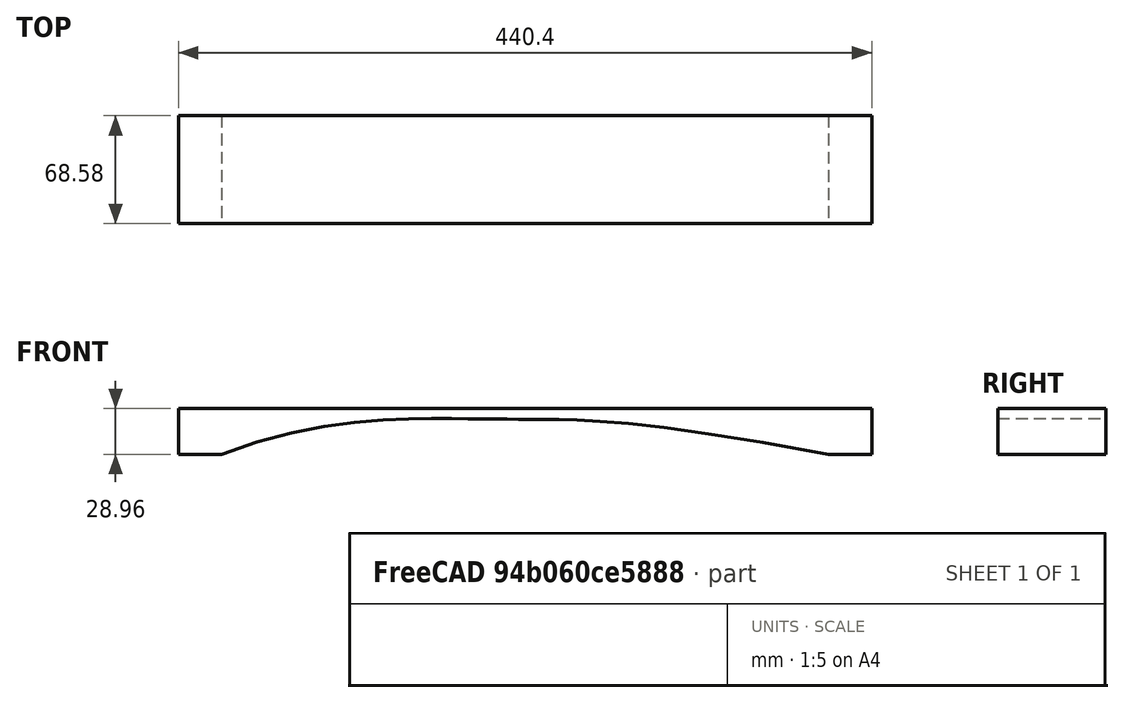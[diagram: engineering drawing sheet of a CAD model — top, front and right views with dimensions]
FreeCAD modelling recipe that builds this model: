
FCSTD DOCUMENT  (FreeCAD 0.20R29410 (Git))
Label: Chestnut-0.82-Bar
License: All rights reserved
LicenseURL: http://en.wikipedia.org/wiki/All_rights_reserved
objects: Fem::FemResultObjectPython×9, Fem::FemPostWarpVectorFilter×3, Fem::FemPostDataAtPointFilter×3, Fem::FemPostPipeline×3, Sketcher::SketchObject×1, Part::Extrusion×1, Fem::FemSolverObjectPython×1, App::MaterialObjectPython×1, Fem::ConstraintDisplacement×1, Fem::FemMeshShapeNetgenObject×1, Fem::FemMeshObjectPython×1, App::TextDocument×1, Fem::FemAnalysis×1
note: 2 computed .brp shape members not serialized (recipe doc carries the construction recipe); baked Part::Feature solids carry a one-line shape summary decoded from their .brp

FEATURE [Sketcher::SketchObject] Sketch
  FullyConstrained = true
  Placement = pos=(0,0,0) rot=(1,0,0;1.5708rad)
  sketch-geometry (12):
    g0: LineSegment StartX=27.53 StartY=0 StartZ=0 EndX=0 EndY=0 EndZ=0
    g1: LineSegment StartX=0 StartY=0 StartZ=0 EndX=0 EndY=28.96 EndZ=0
    g2: LineSegment StartX=0 StartY=28.96 StartZ=0 EndX=440.4 EndY=28.96 EndZ=0
    g3: LineSegment StartX=440.4 StartY=28.96 StartZ=0 EndX=440.4 EndY=0 EndZ=0
    g4: LineSegment StartX=440.4 StartY=0 StartZ=0 EndX=412.87 EndY=0 EndZ=0
    g5-g10: Circle x6 (B-spline internal-alignment scaffolding for g11; pole/knot coordinates omitted)
    g11: BSplineCurve PolesCount=6 KnotsCount=4 Degree=3 IsPeriodic=0
  constraints (38):
    c: DistanceX(g0) = 0
    c: DistanceY(g0) = 0
    c: Distance(g1,g1) = 28.96
    c: Distance(g2,g2) = 440.4
    c: DistanceX(g0,g0) = 27.53
    c: DistanceX(g4,g4) = 27.53
    c: Horizontal(g0)
    c: Vertical(g1)
    c: Horizontal(g2)
    c: Vertical(g3)
    c: Horizontal(g4)
    c: Equal(g3,g1)
    c: Coincident(g0,g1)
    c: Coincident(g1,g2)
    c: Coincident(g2,g3)
    c: Coincident(g3,g4)
    c: DistanceX(g6) = 296.2
    c: DistanceY(g6) = 21.75
    c: DistanceX(g7) = 221.63
    c: DistanceY(g7) = 21.99
    c: DistanceX(g8) = 190.19
    c: DistanceY(g8) = 22.68
    c: DistanceX(g9) = 86.07
    c: DistanceY(g9) = 22.89
    c: Weight(g5) = 1
    c: InternalAlignment(g5,g11)
    c: Weight(g6) = 1
    c: InternalAlignment(g6,g11)
    c: Weight(g7) = 1
    c: InternalAlignment(g7,g11)
    c: Weight(g8) = 1
    c: InternalAlignment(g8,g11)
    c: Weight(g9) = 1
    c: InternalAlignment(g9,g11)
    c: Weight(g10) = 1
    c: InternalAlignment(g10,g11)
    c: Coincident(g4,g11)
    c: Coincident(g0,g11)
FEATURE [Part::Extrusion] Bar
  Base = -> Sketch
  Dir = (0,-1,-3e-16)
  DirMode = 2
  FaceMakerClass = Part::FaceMakerBullseye
  LengthFwd = 68.58
  LengthRev = 0
  Solid = true
  Symmetric = false
FEATURE [Fem::FemSolverObjectPython] SolverCcxTools  # FEM object (typed FeaturePython)
  AnalysisType = 1
  BeamShellResultOutput3D = false
  BucklingFactors = 1
  EigenmodeHighLimit = 20000
  EigenmodeLowLimit = 20
  EigenmodesCount = 12
  GeometricalNonlinearity = 0
  IterationsControlParameterCutb = 0.25,0.5,0.75,0.85,,,1.5,
  IterationsControlParameterIter = 4,8,9,200,10,400,,200,,
  IterationsControlParameterTimeUse = false
  IterationsThermoMechMaximum = 2000
  IterationsUserDefinedIncrementations = false
  IterationsUserDefinedTimeStepLength = false
  MaterialNonlinearity = 0
  MatrixSolverType = 0
  SplitInputWriter = false
  ThermoMechSteadyState = false
  TimeEnd = 1
  TimeInitialStep = 0.01
FEATURE [App::MaterialObjectPython] MaterialSolid  # material (typed FeaturePython)
  Category = 0
  Material = CompressiveStrength=4300 kPa; Density=430 kg/m^3; Name=Wood-Chestnut; PoissonRatio=0.32; ShearModulus=7.4 MPa; UltimateTensileStrength=59.0 MPa; YoungsModulus=8500 MPa
FEATURE [Fem::ConstraintDisplacement] FemConstraintDisplacement
  NormalDirection = (0,3e-16,-1)
  Normals = (118) [(0,3.3e-16,-1),(0,3.3e-16,-1),(0,3.3e-16,-1),(0,3.3e-16,-1),(0,3.3e-16,-1),(0,3.3e-16,-1),(0,3.3e-16,-1),(0,3.3e-16,-1),(0,3.3e-16,-1),(0,3.3e-16,-1),+108 more]
  Points = (118) [(27.53,-68.58,-2.26314e-14),(18.3533,-68.58,-2.26314e-14),(9.17667,-68.58,-2.26314e-14),(0,-68.58,-2.26314e-14),(27.53,-45.72,-1.50876e-14),+113 more]
  References = -> [Bar]
  rotxFix = false
  rotxFree = true
  rotyFix = false
  rotyFree = true
  rotzFix = false
  rotzFree = true
  xDisplacement = 0
  xFix = false
  xFree = true
  xRotation = 0
  yDisplacement = 0
  yFix = true
  yFree = false
  yRotation = 0
  zDisplacement = 0
  zFix = false
  zFree = true
  zRotation = 0
FEATURE [Fem::FemMeshShapeNetgenObject] FEMMeshNetgen
  Fineness = 4
  GrowthRate = 0.3
  MaxSize = 10
  NbSegsPerEdge = 1
  NbSegsPerRadius = 2
  Optimize = true
  SecondOrder = true
  Shape = -> Bar
FEATURE [Fem::FemMeshObjectPython] ResultMesh  # FEM object (typed FeaturePython)
FEATURE [Fem::FemResultObjectPython] CCX_EigenMode_4_Results  # FEM object (typed FeaturePython)
  DisplacementLengths = [66.8075,66.8075,97.2391,97.2391,92.7353,92.7354,104.217,104.217,111.02,111.02,73.6046,73.6047,85.9113,98.3192,106.859,104.538,89.1303,74.1174,59.119,44.0852,29.1952,14.611,5.08468,16.9677,31.471,46.0865,60.4038,74.2639,87.4492,99.5208,+5591 more]
  DisplacementVectors = (5621) [(29.6396,0,59.8727),(29.6396,0,59.8727),(29.6413,0,92.6112),(29.6414,0,92.6112),(-4.79638,0,92.6112),(-4.79642,0,92.6113),(4.97997,0,104.098),+5614 more]
  Eigenmode = 4
  EigenmodeFrequency = 130.83
  MaxShear = [0.793623,0.833442,0.0306815,0.0297045,0.0575452,0.0573412,0.0387805,0.0310506,0.0286361,0.026426,0.681681,0.640425,0.447118,0.128415,0.0679354,0.0973531,0.108643,0.634201,1.60297,3.41101,6.19905,11.583,18.5669,29.2026,45.2438,67.8662,+5595 more]
  Mesh = -> ResultMesh
  NodeNumbers = [1,2,3,4,5,6,7,8,9,10,11,12,13,14,15,16,17,18,19,20,21,22,23,24,25,26,27,28,29,30,31,32,33,34,35,36,37,38,39,40,41,42,43,44,45,46,47,48,49,50,51,52,53,54,55,56,57,58,59,60,61,62,63,64,65,66,67,68,69,+5552 more]
  NodeStrainXX = [0.000162708,0.000169979,-1.07884e-06,-1.07332e-06,-4.70892e-07,-3.62167e-08,8.78541e-07,1.2473e-06,-8.06536e-07,-6.19092e-07,0.000132596,0.000125552,9.50642e-05,2.62909e-05,3.89215e-06,-8.18627e-06,-2.10946e-05,-0.000130126,-0.000334274,+5602 more]
  NodeStrainXY = [-3.87351e-07,-1.91961e-06,6.93051e-07,-5.99991e-07,-1.79433e-07,9.33019e-08,1.69973e-06,-7.83592e-07,-6.94631e-07,8.3591e-07,-5.42509e-07,1.34477e-06,5.06708e-07,6.29561e-09,4.11864e-07,-1.75556e-06,2.84822e-07,1.27065e-06,7.13435e-06,+5602 more]
  NodeStrainXZ = [-2.8685e-05,-2.84597e-05,-4.64503e-06,-4.52092e-06,-8.56091e-06,-8.6366e-06,5.67135e-06,4.67326e-06,4.29e-06,3.89002e-06,3.61949e-05,3.31665e-05,-2.03295e-06,-4.86228e-06,-7.29797e-06,-7.9659e-06,-7.52187e-06,-1.24326e-05,-3.20836e-05,+5602 more]
  NodeStrainYY = [-2.29518e-12,5.81513e-12,0,0,-2.14727e-12,-3.46024e-15,0,0,0,0,-3.38509e-12,-3.00784e-12,2.09083e-07,-5.76141e-07,-6.02025e-08,1.30288e-13,3.25778e-12,1.25115e-07,3.93909e-07,-2.69759e-11,2.80364e-11,-2.59318e-05,-9.41e-06,-1.5324e-05,+5597 more]
  NodeStrainYZ = [-3.50751e-07,-1.51215e-06,-4.74264e-07,3.68907e-07,6.61863e-08,-1.53237e-08,-2.48968e-07,6.46807e-07,-5.76628e-07,6.47043e-07,1.21666e-06,-1.60203e-07,-6.62246e-07,-6.41747e-07,7.67443e-07,1.53127e-06,-2.16566e-06,8.19819e-07,-4.53612e-06,+5602 more]
  NodeStrainZZ = [-7.70098e-05,-8.249e-05,-1.86474e-06,-1.84357e-06,4.64207e-06,4.29724e-06,2.49195e-06,1.6006e-06,-1.84808e-06,-1.67572e-06,-6.63414e-05,-6.19546e-05,-4.37331e-05,-1.23557e-05,-1.12699e-05,1.71027e-05,8.6202e-06,6.52526e-05,0.000159143,+5602 more]
  NodeStressXX = [1.53827,1.59534,-0.0237959,-0.0236076,0.0208432,0.0241565,0.0249496,0.024333,-0.0203884,-0.0171219,1.23307,1.1725,0.907168,0.245764,-0.0175109,-0.00167765,-0.207238,-1.20854,-3.1527,-6.65105,-12.3436,-22.519,-36.3695,-57.4007,-89.5534,+5596 more]
  NodeStressXY = [-0.00249431,-0.0123611,0.00446283,-0.00386358,-0.00115544,0.000600808,0.0109452,-0.00504586,-0.00447301,0.00538275,-0.00349343,0.00865947,0.00326289,4.05399e-05,0.00265215,-0.0113047,0.00183408,0.00818224,0.0459409,-0.0196225,-0.071634,+5600 more]
  NodeStressXZ = [-0.184714,-0.183263,-0.0299112,-0.029112,-0.0551271,-0.0556144,0.03652,0.0300929,0.027625,0.0250493,0.233073,0.213572,-0.013091,-0.0313101,-0.0469945,-0.0512956,-0.0484363,-0.0800581,-0.206599,-0.107018,-0.383565,-2.88037,-5.68835,-8.86154,+5597 more]
  NodeStressYY = [0.490529,0.500779,-0.0168488,-0.016696,0.0238754,0.0243897,0.0192924,0.0163011,-0.0151948,-0.0131353,0.379234,0.364024,0.296358,0.0727561,-0.0429617,0.051037,-0.071402,-0.369807,-0.997644,-2.07487,-3.94135,-7.45487,-12.0454,-19.0587,+5597 more]
  NodeStressYZ = [-0.00225863,-0.00973732,-0.00305397,0.00237554,0.000426199,-9.86756e-05,-0.0016032,0.00416505,-0.00371313,0.00416657,0.00783455,-0.00103161,-0.00426446,-0.00413246,0.00494186,0.00986046,-0.0139455,0.00527914,-0.0292099,0.0309938,-0.114886,+5600 more]
  NodeStressZZ = [-0.00536748,-0.0304064,-0.0288566,-0.0285675,0.0537675,0.0520614,0.035339,0.026608,-0.0270953,-0.0239259,-0.0479645,-0.0349264,0.0133971,-0.00309685,-0.115145,0.161168,-0.0158931,0.0495748,0.0246048,0.167091,0.0268859,-0.0886269,-1.02233,+5598 more]
  PrincipalMax = [1.56007,1.61586,0.0050034,0.00408445,0.094853,0.0954496,0.0677832,0.0555914,0.00570159,0.00704383,1.27416,1.20925,0.907378,0.249644,0.00144179,0.177242,-0.00152922,0.0547019,0.0389779,0.169207,0.0419516,0.28008,-0.129444,-0.373552,-0.60558,+5596 more]
  PrincipalMed = [0.490537,0.500887,-0.0181452,-0.0176311,0.0238706,0.0243908,0.0215756,0.0181607,-0.0168095,-0.0154187,0.379377,0.363955,0.296403,0.0729643,-0.0426304,0.0507493,-0.0741891,-0.369775,-0.997749,-2.07523,-3.94386,-7.45675,-12.0446,-19.0577,+5597 more]
  PrincipalMin = [-0.0271753,-0.0510299,-0.0563595,-0.0553245,-0.0202375,-0.0192328,-0.00977786,-0.00650993,-0.0515706,-0.0458083,-0.0892001,-0.0716043,0.0131426,-0.00718552,-0.134429,-0.0174641,-0.218815,-1.2137,-3.16697,-6.65281,-12.3562,-22.8858,-37.2631,+5598 more]
  ResultType = Fem::ResultMechanical
  Stats = [-38.5889,29.6414,-0.00115149,0.000609511,-137.504,104.098,0.662442,137.504,0.011057,499.611,-9.6242,564.832,-179.962,180.829,-562.552,8.4389,0.00626612,282.416,0,0,0,0,0,0,0,0]
  Time = 0
  vonMises = [1.40201,1.47076,0.0536731,0.0520662,0.100573,0.100261,0.0675792,0.0541584,0.049976,0.0459425,1.19978,1.12801,0.791575,0.227598,0.120063,0.17112,0.191584,1.11831,2.83358,6.02211,10.9628,20.4276,32.8394,51.6625,80.0872,120.138,173.48,239.494,+5593 more]
FEATURE [Fem::FemResultObjectPython] CCX_EigenMode_5_Results  # FEM object (typed FeaturePython)
  DisplacementLengths = [46.678,46.6778,83.7234,83.7237,82.1591,82.1595,93.0927,93.0918,101.742,101.741,55.1361,55.1365,68.8818,84.675,94.5431,91.5012,72.0663,51.5312,32.1795,18.2149,23.3378,40.651,60.2468,79.8832,98.852,116.49,131.696,143.334,150.029,150.411,+5591 more]
  DisplacementVectors = (5621) [(24.1944,0,39.9183),(24.1945,0,39.918),(24.2175,0,80.1444),(24.2177,0,80.1446),(-18.0814,0,80.1447),(-18.0818,0,80.1451),(-17.4443,0,-91.4437),+5614 more]
  Eigenmode = 5
  EigenmodeFrequency = 522.972
  MaxShear = [10.5108,10.9922,0.413182,0.401906,0.774139,0.771511,0.514913,0.416264,0.387636,0.358172,9.60448,9.12995,6.56095,2.02485,0.947608,1.29303,1.81745,9.01506,21.2038,42.6378,73.3258,127.307,191.684,282.312,406.01,560.303,736.915,914.833,1058.39,+5592 more]
  Mesh = -> ResultMesh
  NodeNumbers = <same value as first occurrence — deduplicated (x9 in doc)>
  NodeStrainXX = [0.00215714,0.00224604,-1.29996e-05,-1.29881e-05,-9.04107e-06,-3.23626e-06,-8.62545e-06,-1.35011e-05,8.0887e-06,5.68333e-06,-0.00187511,-0.0017941,-0.00139597,-0.00041764,-5.09876e-05,0.000103216,0.000362657,0.00185832,0.00443468,0.00890026,+5601 more]
  NodeStrainXY = [-4.39638e-06,-2.36403e-05,9.73128e-06,-8.50894e-06,-2.26535e-06,1.03915e-06,-2.26738e-05,1.11262e-05,1.00137e-05,-1.16842e-05,7.07931e-06,-1.56076e-05,-4.70013e-06,2.64272e-07,-6.00863e-06,2.53601e-05,-3.82025e-06,-1.63301e-05,-8.47599e-05,+5602 more]
  NodeStrainXZ = [-0.000372628,-0.000366394,-6.23753e-05,-6.09899e-05,-0.000114446,-0.000115587,-7.48349e-05,-6.24315e-05,-5.76267e-05,-5.23151e-05,-0.000504932,-0.00046796,3.30998e-05,7.08549e-05,0.00010586,0.000110984,0.000110296,0.000169579,0.000399203,+5602 more]
  NodeStrainYY = [-2.94739e-11,6.69036e-11,0,0,-2.87809e-11,-4.37756e-13,0,0,0,0,4.55109e-11,3.35361e-11,-2.89534e-06,7.49746e-06,1.25697e-06,-1.17436e-12,-4.3669e-11,-4.93314e-07,-4.35375e-06,3.08363e-10,-2.79477e-10,0.000255873,8.35823e-05,0.000122951,+5597 more]
  NodeStrainYZ = [-3.4348e-06,-1.81779e-05,-6.1324e-06,4.74999e-06,8.95644e-07,-1.13147e-08,2.51341e-06,-8.03233e-06,7.4803e-06,-8.29467e-06,-1.67216e-05,5.96487e-06,8.21289e-06,8.94771e-06,-1.17966e-05,-1.97864e-05,2.77119e-05,-1.10977e-05,5.0911e-05,+5602 more]
  NodeStrainZZ = [-0.00102115,-0.00108785,-2.64677e-05,-2.62991e-05,6.44198e-05,5.9793e-05,-3.60283e-05,-2.45201e-05,2.74303e-05,2.51771e-05,0.000931459,0.000882452,0.00064059,0.000194661,0.000152165,-0.000225297,-0.000152197,-0.000920775,-0.00209941,+5602 more]
  NodeStressXX = [20.393,21.0925,-0.309616,-0.308512,0.258764,0.302886,-0.311136,-0.304569,0.255394,0.213239,-17.4759,-16.7711,-13.3295,-3.92274,0.257994,-0.034133,3.53994,17.33,41.8987,83.4443,146.231,249.206,378.428,558.888,807.49,1119.11,1474.71,1830.72,+5593 more]
  NodeStressXY = [-0.02831,-0.152229,0.0626635,-0.0547924,-0.0145875,0.00669149,-0.146005,0.0716458,0.0644823,-0.0752389,0.0455865,-0.100503,-0.030266,0.00170175,-0.0386919,0.163304,-0.0246001,-0.105156,-0.545802,0.271795,0.716407,-1.76691,1.62758,2.04468,+5597 more]
  NodeStressXZ = [-2.3995,-2.35935,-0.401659,-0.392738,-0.736963,-0.744309,-0.481892,-0.402021,-0.371081,-0.336878,-3.25145,-3.01338,0.213142,0.456263,0.681676,0.714672,0.71024,1.09199,2.57062,1.36702,4.20481,28.7135,52.5566,75.4304,90.4039,98.8392,97.4473,+5594 more]
  NodeStressYY = [6.50229,6.62938,-0.225907,-0.224876,0.316982,0.323725,-0.255594,-0.21763,0.203307,0.176642,-5.40135,-5.21817,-4.35895,-1.18512,0.594418,-0.69878,1.20465,5.36041,13.3139,26.132,46.7483,82.3124,124.931,184.626,263.207,362.917,476.159,588.431,+5593 more]
  NodeStressYZ = [-0.0221181,-0.117054,-0.0394889,0.0305871,0.00576741,-7.286e-05,0.0161848,-0.0517233,0.0481686,-0.0534126,-0.107677,0.0384101,0.052886,0.0576178,-0.0759629,-0.127413,0.178448,-0.0714627,0.327836,-0.354072,1.22421,-2.15312,0.131867,0.104255,+5597 more]
  NodeStressZZ = [-0.0733022,-0.375692,-0.396343,-0.394227,0.731807,0.708756,-0.487594,-0.375525,0.379941,0.338768,0.596681,0.464282,-0.215288,0.0201036,1.56617,-2.14956,0.224595,-0.565643,-0.176936,-1.78169,-0.142689,1.22329,9.76238,14.8022,15.861,16.0807,+5595 more]
  PrincipalMax = [20.6706,21.35,0.0690939,0.0570042,1.26946,1.27732,0.130114,0.0886953,0.693987,0.618793,1.16583,0.976425,-0.211163,0.0748319,1.86252,0.200581,3.68574,17.3974,42.0648,83.4675,146.357,252.511,385.784,569.163,817.687,1127.9,1481.18,1834.51,+5593 more]
  PrincipalMed = [6.50234,6.6305,-0.243691,-0.237811,0.316916,0.323754,-0.284726,-0.242586,0.225939,0.207407,-5.40327,-5.21794,-4.3595,-1.18773,0.588767,-0.697567,1.2326,5.36012,13.3138,26.1354,46.7734,82.3334,124.921,184.615,263.203,362.915,476.159,588.433,+5593 more]
  PrincipalMin = [-0.350952,-0.634354,-0.757269,-0.746808,-0.27882,-0.265704,-0.899712,-0.743833,-0.0812843,-0.0975508,-18.0431,-17.2835,-13.3331,-3.97486,-0.0327012,-2.38549,0.0508447,-0.632734,-0.342922,-1.80821,-0.294153,-2.10251,2.41627,4.53821,5.66765,+5596 more]
  ResultType = Fem::ResultMechanical
  Stats = [-18.193,44.6047,-0.00546583,0.00337327,-116.271,151.067,0.326805,151.271,0.276706,2018.52,-41.4924,2260.55,-738.671,729.831,-2287,50.4867,0.153202,1140.91,0,0,0,0,0,0,0,0]
  Time = 0
  vonMises = [18.569,19.4005,0.722659,0.704311,1.35266,1.34864,0.897453,0.725982,0.676203,0.62265,16.9101,16.0837,11.6172,3.58902,1.6734,2.27415,3.21146,15.9043,37.4936,75.2986,129.69,224.63,339.137,499.552,718.732,991.824,1304.23,1618.79,1872.32,+5592 more]
FEATURE [Fem::FemResultObjectPython] CCX_EigenMode_6_Results  # FEM object (typed FeaturePython)
  DisplacementLengths = [40.6343,40.6333,77.5711,77.5724,73.3747,73.3768,76.7356,76.7315,85.3124,85.309,44.855,44.8545,55.2761,69.3229,77.45,74.3735,56.5398,37.3781,21.8513,20.7638,34.9905,52.6363,70.1082,85.5972,97.6207,104.22,102.896,91.183,67.2291,32.0267,+5591 more]
  DisplacementVectors = (5621) [(-29.8014,0,-27.6229),(-29.8015,0,-27.6213),(-29.9373,0,-71.5614),(-29.9383,0,-71.5624),(16.2034,0,-71.5632),(16.2055,0,-71.5649),+5615 more]
  Eigenmode = 6
  EigenmodeFrequency = 1308.65
  MaxShear = [59.9364,62.4101,2.26326,2.20937,4.24288,4.22841,2.54466,2.06947,1.93641,1.79073,49.222,47.0789,34.3919,11.0304,4.81285,6.38982,9.93686,45.957,104.112,202.52,335.954,553.253,792.274,1100.89,1471.16,1851.07,2162.83,2292.67,2120.07,1586.87,+5591 more]
  Mesh = -> ResultMesh
  NodeNumbers = <same value as first occurrence — deduplicated (x9 in doc)>
  NodeStrainXX = [-0.0123109,-0.0127713,6.45248e-05,6.46694e-05,6.14133e-05,2.98644e-05,-3.38797e-05,-5.79059e-05,3.23931e-05,2.07907e-05,-0.00962868,-0.00926281,-0.00732013,-0.0022834,-0.000249744,0.00049405,0.00199832,0.00949426,0.0218093,0.0423238,+5601 more]
  NodeStrainXY = [2.1812e-05,0.000124048,-5.50543e-05,4.85482e-05,1.18602e-05,-4.78924e-06,-0.000112278,5.7019e-05,5.16912e-05,-5.93618e-05,3.49221e-05,-7.08311e-05,-1.72495e-05,2.28388e-06,-3.12083e-05,0.000131121,-1.89789e-05,-7.91446e-05,-0.000390441,+5602 more]
  NodeStrainXZ = [0.0020952,0.00204476,0.000340748,0.000334338,0.00062387,0.000630565,-0.000368227,-0.000309407,-0.000286347,-0.000260141,-0.0025748,-0.00240128,0.000179221,0.000368012,0.000548483,0.000562962,0.000574448,0.000850788,0.00189684,0.00102492,+5601 more]
  NodeStrainYY = [1.62443e-10,-3.16358e-10,0,0,1.57489e-10,4.05779e-12,0,0,0,0,2.29892e-10,1.51218e-10,-1.4663e-05,3.65562e-05,7.53357e-06,-4.1989e-12,-2.16872e-10,9.01673e-07,-1.89946e-05,1.38224e-09,-1.11947e-09,0.00101613,0.000298495,0.000388624,+5597 more]
  NodeStrainYZ = [1.44708e-05,9.34811e-05,3.24726e-05,-2.50562e-05,-5.00258e-06,-7.60733e-07,1.01528e-05,-3.80486e-05,3.64531e-05,-4.01057e-05,-8.43089e-05,4.0107e-05,3.89765e-05,4.53619e-05,-6.28539e-05,-9.61281e-05,0.000133901,-5.54432e-05,0.000224988,+5602 more]
  NodeStrainZZ = [0.00582683,0.00617343,0.0001508,0.00015039,-0.000361762,-0.000336438,-0.000186373,-0.000130463,0.000143709,0.000132649,0.00476404,0.00454715,0.00335509,0.00106053,0.000758399,-0.00110745,-0.000845977,-0.00467639,-0.010291,-0.020539,+5601 more]
  NodeStressXX = [-116.389,-120.005,1.648,1.64741,-1.3237,-1.56249,-1.47887,-1.45109,1.21658,1.01215,-89.8476,-86.6389,-69.9166,-21.4941,1.34641,-0.329673,19.4638,88.7195,206.26,397.233,670.667,1088.19,1572.94,2190.92,2936.14,3702.73,4324.77,4570.87,4202.6,+5592 more]
  NodeStressXY = [0.140456,0.798792,-0.354516,0.312621,0.0763723,-0.0308398,-0.723005,0.367168,0.33286,-0.382254,0.224877,-0.456109,-0.111076,0.0147068,-0.200963,0.844342,-0.122213,-0.509643,-2.5142,1.37468,2.8772,-6.8438,7.26639,8.06262,5.63206,5.00116,+5595 more]
  NodeStressXZ = [13.4918,13.167,2.19421,2.15293,4.01735,4.06046,-2.37116,-1.99239,-1.8439,-1.67515,-16.5801,-15.4628,1.15407,2.36978,3.5319,3.62513,3.6991,5.47856,12.2145,6.59987,18.2539,115.103,195.791,256.973,272.561,248.927,180.859,72.8199,-55.4058,+5592 more]
  NodeStressYY = [-37.1145,-37.7657,1.2325,1.23098,-1.71917,-1.7548,-1.26071,-1.07821,1.00799,0.878272,-27.8448,-26.992,-22.8739,-6.55495,3.00312,-3.51106,6.59587,27.588,65.6987,124.694,214.579,358.826,517.908,720.399,952.448,1194.09,1387.16,1457.48,1331.21,+5592 more]
  NodeStressYZ = [0.0931833,0.601961,0.209104,-0.161347,-0.0322136,-0.00489866,0.0653781,-0.24501,0.234736,-0.258256,-0.542898,0.258265,0.250985,0.292103,-0.404741,-0.619007,0.86224,-0.35702,1.44879,-1.58671,5.19859,-8.6274,0.814122,0.697053,2.28917,3.29718,+5595 more]
  NodeStressZZ = [0.406793,1.98747,2.20356,2.1994,-4.0487,-3.92126,-2.46084,-1.91831,1.93339,1.73245,2.83275,2.28893,-1.17467,0.0388313,7.83824,-10.6424,1.14829,-2.53096,-0.446707,-7.56485,-0.106803,6.15014,37.5894,50.0026,44.7756,34.2261,14.2814,-12.1461,+5593 more]
  PrincipalMax = [1.94536,3.40378,4.1396,4.09652,1.55648,1.48663,0.645059,0.446743,3.45378,3.08645,5.71935,4.90432,-1.15244,0.30897,9.42098,0.904806,20.1828,89.0518,207.021,397.347,671.183,1100.38,1597.56,2221.38,2961.63,3719.55,4332.35,4572.03,4203.33,+5592 more]
  PrincipalMed = [-37.1146,-37.7707,1.33138,1.30348,-1.71878,-1.75499,-1.40121,-1.20217,1.12322,1.03144,-27.8543,-26.9928,-22.8765,-6.56735,2.97151,-3.51311,6.71604,27.5869,65.6951,124.707,214.681,358.915,517.859,720.356,952.434,1194.09,1387.16,1457.49,+5593 more]
  PrincipalMin = [-117.927,-121.416,-0.386922,-0.322212,-6.92927,-6.97019,-4.44427,-3.69219,-0.419041,-0.495017,-92.7247,-89.2535,-69.9363,-21.7518,-0.20472,-11.8748,0.309095,-2.8622,-1.20397,-7.69198,-0.724872,-6.12803,13.015,19.5902,19.3031,17.4048,+5595 more]
  ResultType = Fem::ResultMechanical
  Stats = [-29.9397,41.8053,-0.0190391,0.0165747,-204.05,105.095,0.936558,204.077,1.79422,4433.1,-112.126,4932.44,-1615.12,1582.27,-5014.46,118.316,1.00547,2506.29,0,0,0,0,0,0,0,0]
  Time = 0
  vonMises = [105.891,110.164,3.95778,3.87099,7.41231,7.39,4.43557,3.60901,3.37705,3.11288,86.6792,82.9443,60.9006,19.5516,8.49524,11.2418,17.5694,81.0965,184.128,357.714,594.245,976.571,1402.04,1948.33,2604.31,3276.32,3826.95,4055.18,3748.28,2803.59,+5591 more]
FEATURE [Fem::FemResultObjectPython] CCX_EigenMode_7_Results  # FEM object (typed FeaturePython)
  DisplacementLengths = [33.6773,33.6729,78.7579,78.7613,79.5016,79.5078,69.7298,69.7194,78.8889,78.8802,42.2924,42.2869,50.2126,63.2348,70.1279,66.7861,49.4471,30.9029,19.5256,26.3737,42.3134,58.6057,72.3591,80.9079,81.6197,71.4418,48.2709,19.8217,51.8057,107.309,+5591 more]
  DisplacementVectors = (5621) [(26.2857,0,21.0529),(26.2849,0,21.0468),(26.7171,0,74.0878),(26.7199,0,74.0904),(-28.8204,0,74.0938),(-28.8266,0,74.098),(-19.981,0,-66.8057),+5614 more]
  Eigenmode = 7
  EigenmodeFrequency = 2348.85
  MaxShear = [189.976,197.495,7.4125,7.26689,13.8035,13.8482,7.17114,5.86498,5.54379,5.11145,143.324,137.786,102.1,33.6997,13.925,17.9978,30.1904,132.657,291.405,550.422,882.501,1378.72,1871.49,2433.09,2968.06,3289.97,3183.92,2445.53,1064.34,1155.42,+5591 more]
  Mesh = -> ResultMesh
  NodeNumbers = <same value as first occurrence — deduplicated (x9 in doc)>
  NodeStrainXX = [0.0390514,0.0404711,-0.000188927,-0.000187972,-0.000239557,-0.000136768,-6.98446e-05,-0.000143671,7.10668e-05,4.34308e-05,-0.028079,-0.0271371,-0.0217363,-0.00699623,-0.000699389,0.00135161,0.00609982,0.0274538,0.0611281,0.115152,0.186165,+5600 more]
  NodeStrainXY = [-5.79005e-05,-0.000370681,0.000181584,-0.000161714,-4.19469e-05,1.16501e-05,-0.000317554,0.000162908,0.000150804,-0.000172495,9.77248e-05,-0.000186056,-3.26196e-05,1.1617e-05,-9.33545e-05,0.000383367,-5.69079e-05,-0.000217344,-0.0010337,+5602 more]
  NodeStrainXZ = [-0.00653802,-0.00634631,-0.00111341,-0.00109608,-0.0020171,-0.0020556,-0.00103234,-0.000874819,-0.00081544,-0.000739909,-0.00747294,-0.00699932,0.000539287,0.00108337,0.00161601,0.00162017,0.00168776,0.00243337,0.00515688,0.00283215,+5601 more]
  NodeStrainYY = [-4.93268e-10,9.94886e-10,0,0,-5.20067e-10,-1.90226e-11,0,0,0,0,6.54281e-10,3.54831e-10,-4.2799e-05,0.000103768,2.62539e-05,-4.27737e-12,-5.893e-10,7.93393e-06,-4.98723e-05,3.57219e-09,-2.49448e-09,0.00228468,0.000583542,0.000625228,+5597 more]
  NodeStrainYZ = [-2.63956e-05,-0.000273421,-0.000102829,8.28373e-05,1.70908e-05,6.22165e-06,2.60574e-05,-0.000102113,0.000103655,-0.000107036,-0.000239659,0.0001374,0.000107046,0.000130619,-0.000184834,-0.000265576,0.00036818,-0.000156987,0.000566554,+5602 more]
  NodeStrainZZ = [-0.0184857,-0.0195334,-0.000513044,-0.00051572,0.00120869,0.00112681,-0.000546123,-0.000390367,0.000427721,0.000391539,0.0138468,0.0133003,0.00995526,0.00323836,0.00215189,-0.00310504,-0.00259807,-0.0134561,-0.0287596,-0.0556988,-0.0875183,+5600 more]
  NodeStressXX = [369.183,380.454,-5.23459,-5.2383,4.00463,4.78622,-3.9755,-3.98195,3.31264,2.76939,-262.276,-253.947,-207.647,-65.9673,3.96063,-1.33292,59.3228,256.953,578.616,1081.81,1763.43,2724.06,3734.77,4864.19,5937.84,6575.47,6324.93,4767.34,1791.21,+5592 more]
  NodeStressXY = [-0.372844,-2.38696,1.16929,-1.04134,-0.270112,0.0750198,-2.04485,1.04903,0.971087,-1.11077,0.629289,-1.19809,-0.21005,0.0748061,-0.601146,2.46865,-0.366452,-1.39956,-6.65643,3.95228,6.55392,-14.9855,18.3168,17.859,11.5496,8.81248,6.00431,+5594 more]
  NodeStressXZ = [-42.1009,-40.8664,-7.1697,-7.05806,-12.9889,-13.2368,-6.64766,-5.63331,-5.25094,-4.76456,-48.1212,-45.0714,3.47268,6.97623,10.4062,10.4329,10.8681,15.6695,33.2072,18.2373,45.3972,261.969,406.635,470.745,406.566,241.813,-3.93884,-274.036,+5593 more]
  NodeStressYY = [117.716,119.845,-4.01802,-4.02787,5.54723,5.66692,-3.52574,-3.05679,2.85502,2.48973,-81.4636,-79.2002,-67.954,-20.2476,8.63333,-10.0365,20.0437,80.2181,184.668,340.304,564.644,896.68,1226.12,1590.67,1914.47,2103.99,2006.37,1492.24,533.456,+5592 more]
  NodeStressYZ = [-0.169971,-1.76067,-0.662154,0.533422,0.110055,0.0400637,0.167794,-0.657546,0.667476,-0.689247,-1.54326,0.88477,0.689314,0.84111,-1.19022,-1.71015,2.37086,-1.0109,3.64826,-4.06843,12.6235,-19.6271,2.56481,2.1511,5.45719,7.05387,7.54889,+5594 more]
  NodeStressZZ = [-1.32113,-5.93795,-7.32171,-7.3488,13.3305,12.9229,-7.04245,-5.57052,5.60928,5.011,7.70168,6.44577,-3.57258,-0.062739,22.3212,-30.0311,3.31364,-6.48241,-0.205553,-18.3626,1.07987,17.3725,81.3525,90.0483,57.7295,13.3662,-42.864,-92.8836,+5593 more]
  PrincipalMax = [373.907,384.747,1.29417,1.09558,22.4716,22.7025,1.86197,1.25965,9.83715,8.78845,16.0496,14.0388,-3.50621,0.701655,27.1138,2.33,61.3579,257.894,580.62,1082.13,1764.64,2749.33,3779.62,4910.26,5965.85,6584.39,6324.94,4782.75,1906.56,53.9358,+5591 more]
  PrincipalMed = [117.716,119.858,-4.33766,-4.27234,5.546,5.66758,-3.92535,-3.3986,3.19021,2.91611,-81.4901,-79.2066,-67.9609,-20.2816,8.53767,-10.0649,20.3451,80.2159,184.65,340.331,564.879,896.89,1225.99,1590.57,1914.45,2103.99,2006.39,1492.26,533.475,+5592 more]
  PrincipalMin = [-6.04525,-10.2436,-13.5308,-13.4382,-5.13529,-4.994,-12.4803,-10.4703,-1.25042,-1.43444,-270.597,-261.534,-207.706,-66.6977,-0.736288,-33.6656,0.977162,-7.42097,-2.19105,-18.7124,-0.363142,-8.11163,36.6399,44.074,29.7401,4.44594,-42.8943,+5594 more]
  ResultType = Fem::ResultMechanical
  Stats = [-28.8337,41.9642,-0.0387734,0.0352282,-196.016,179.752,0.966456,196.052,8.52357,8120.95,-300.369,8825.35,-2947.82,2837.33,-9180.32,317.344,4.78018,4591.4,0,0,0,0,0,0,0,0]
  Time = 0
  vonMises = [335.645,348.648,12.9617,12.7291,24.1113,24.1966,12.4976,10.2299,9.66528,8.88592,252.43,242.774,180.805,59.7387,24.5632,31.6726,53.3994,234.138,515.446,972.379,1561.11,2434.55,3312.51,4306.49,5253.73,5821.41,5630.22,4319.24,1869.17,2039.22,+5591 more]
FEATURE [Fem::FemResultObjectPython] CCX_EigenMode_8_Results  # FEM object (typed FeaturePython)
  DisplacementLengths = [43.9267,43.9286,61.339,61.3445,88.3218,88.2976,115.177,115.209,75.5335,75.5607,47.5308,47.5515,53.3867,63.2688,87.2785,100.663,106.821,100.648,96.8843,95.4772,95.7388,96.2274,95.2351,90.4856,80.1904,64.2505,49.5829,54.4996,78.3633,99.049,+5591 more]
  DisplacementVectors = (5621) [(42.3885,0,-11.5226),(42.3681,0,-11.6046),(42.2535,0,-44.4648),(42.2796,0,-44.4475),(76.3108,0,-44.468),(76.2723,0,-44.4859),(-98.5656,0,-59.5862),+5614 more]
  Eigenmode = 8
  EigenmodeFrequency = 3420.72
  MaxShear = [118.315,107.914,9.76756,9.34847,22.4206,16.3549,12.5438,10.4139,12.6318,10.5489,121.864,118.505,59.8356,22.1125,27.9925,31.3519,137.217,399.778,737.482,1200.75,1735.21,2419.66,3056.66,3664.09,4038.85,4044.85,3462.96,2287.32,836.912,724.996,+5591 more]
  Mesh = -> ResultMesh
  NodeNumbers = <same value as first occurrence — deduplicated (x9 in doc)>
  NodeStrainXX = [-0.0243224,-0.0221876,0.000370186,0.000523525,0.00011844,-1.81183e-05,0.000134906,-0.000383903,3.82248e-05,0.000258224,-0.0236498,-0.0232241,-0.0124521,0.00353757,-0.00139662,0.00231554,0.0289526,0.0838077,0.155657,0.252315,0.366476,+5600 more]
  NodeStrainXY = [6.6447e-05,0.000303329,-0.000483859,0.000382605,-0.000292735,-8.13439e-05,-0.00058843,0.00011501,0.000267094,-0.000396108,-0.00010049,-0.000262363,-7.08652e-05,0.000206622,-0.000276631,0.000648273,-0.000291519,-0.00021714,-0.00161449,+5602 more]
  NodeStrainXZ = [0.00363769,0.00258747,0.00140832,0.00139999,0.00337013,0.00244775,-0.0017366,-0.00159745,-0.00184452,-0.00157849,-0.00619994,-0.0050221,0.00197436,0.00204799,0.00339369,0.00280756,0.00290231,0.00427242,0.00689854,0.00415595,0.00853905,+5600 more]
  NodeStrainYY = [9.54335e-10,6.06636e-09,0,0,2.04297e-10,2.48275e-12,0,0,0,0,-1.7897e-09,-4.17012e-09,-9.898e-05,0.000328621,0.000151014,2.48202e-10,5.85687e-10,-0.000152168,-0.000246885,5.8929e-09,4.02276e-10,0.0022177,0.000465816,0.000360831,-0.000952846,+5596 more]
  NodeStrainYZ = [0.000126766,0.00011547,0.000135585,0.000134079,3.10159e-05,5.98397e-05,0.000233212,-0.000119875,0.000320759,4.40033e-05,-0.000203241,0.00038725,0.000192294,0.000266546,-0.000116344,-0.000405016,0.000510858,-0.000201418,0.00058019,+5602 more]
  NodeStrainZZ = [0.0116956,0.0109216,0.000574601,0.00041617,-0.00152377,-0.00136087,-0.000995909,-0.000687267,0.000987239,0.000586913,0.0121076,0.0121692,0.00570132,-0.00193523,0.00400196,-0.00548317,-0.013245,-0.0400626,-0.0729587,-0.120524,-0.172158,+5600 more]
  NodeStressXX = [-228.896,-207.36,7.79164,8.74992,-7.28128,-8.00989,-4.05959,-8.60337,6.1158,6.50029,-218.356,-212.826,-119.392,33.8325,6.78367,-3.22058,276.347,789.193,1474.28,2379.11,3472.15,4824.46,6130.82,7337.2,8077.81,8032.12,6789.83,4338.97,1224.03,+5592 more]
  NodeStressXY = [0.427878,1.95325,-3.11576,2.46374,-1.88504,-0.523805,-3.78913,0.740597,1.71992,-2.5507,-0.647098,-1.68946,-0.456329,1.33052,-1.78134,4.17448,-1.87721,-1.39825,-10.3963,5.85572,7.68132,-12.7543,23.2781,23.188,9.64202,5.78111,0.444052,+5594 more]
  NodeStressXZ = [23.4245,16.6617,9.06872,9.01506,21.7016,15.762,-11.1827,-10.2866,-11.8776,-10.1645,-39.9239,-32.3393,12.7137,13.1878,21.8533,18.079,18.6891,27.5118,44.4224,26.7618,54.9863,269.241,369.124,348.21,170.463,-84.1302,-356.653,-540.195,-534.924,+5592 more]
  NodeStressYY = [-72.2742,-64.4851,5.40787,5.37873,-8.04396,-7.89321,-4.9283,-6.13127,5.86966,4.83749,-66.066,-63.2772,-39.845,13.1688,16.7495,-18.1312,89.9092,248.542,470.355,754.357,1112.26,1567.64,1985.78,2364.51,2579.15,2550.29,2135.64,1348.12,365.754,+5592 more]
  NodeStressYZ = [0.816295,0.743557,0.873084,0.863387,0.199723,0.385331,1.50174,-0.771924,2.06549,0.283354,-1.30875,2.49366,1.23825,1.7164,-0.749184,-2.60806,3.28962,-1.29701,3.73607,-3.92833,13.6431,-20.5641,2.83154,1.5133,7.45246,7.23765,6.69613,3.40582,+5593 more]
  NodeStressZZ = [3.03863,5.84359,9.10795,8.05862,-17.8561,-16.6564,-11.3414,-10.5569,12.2269,8.61685,11.8998,15.0853,-2.49457,-1.40905,41.5473,-53.4395,4.6197,-8.45664,2.13527,-21.7446,3.66568,15.5072,62.3674,42.2976,7.35469,-55.8027,-99.2352,-106.254,+5593 more]
  PrincipalMax = [5.39017,7.14896,17.7276,17.8791,9.87105,4.01381,5.55323,0.914409,21.4575,18.0593,18.6422,19.6733,-1.09174,38.3505,52.1478,3.09014,277.641,790.145,1475.72,2379.43,3473.05,4839.55,6153.32,7353.89,8081.43,8033,6808.25,4403.67,1417.32,89.5805,+5591 more]
  PrincipalMed = [-72.2829,-64.4715,6.38745,5.12604,-8.0823,-7.8773,-6.34824,-6.29256,6.56084,4.9338,-66.0779,-63.3538,-39.8768,13.1163,16.7698,-18.2678,90.0289,248.544,470.285,754.357,1112.4,1567.83,1985.65,2364.4,2579.15,2550.3,2135.66,1348.13,365.888,+5592 more]
  PrincipalMin = [-231.239,-208.679,-1.80756,-0.817853,-34.9701,-28.696,-19.5343,-19.9134,-3.80602,-3.03845,-225.087,-217.337,-120.763,-5.87457,-3.83712,-59.6137,3.20617,-9.41046,0.761135,-22.0634,2.62947,0.229374,39.9962,25.714,3.73541,-56.6982,-117.67,+5594 more]
  ResultType = Fem::ResultMechanical
  Stats = [-98.5968,76.3169,-0.0710913,0.111141,-94.5638,104.564,1.24885,115.215,12.0916,11520.7,-1391.72,13028.4,-1788.55,4199.88,-3327.73,458.839,6.9525,6512.3,0,0,0,0,0,0,0,0]
  Time = 0
  vonMises = [208.918,190.404,16.9908,16.5461,39.0897,28.6771,21.7359,18.3203,21.9958,18.4519,214.319,208.301,105.755,38.427,49.0437,55.2151,242.951,706.81,1305.16,2122.6,3069.86,4276.71,5409.61,6483.31,7146.92,7151.91,6118.78,4035.55,1465.36,1276.18,+5591 more]
FEATURE [Fem::FemResultObjectPython] CCX_EigenMode_9_Results  # FEM object (typed FeaturePython)
  DisplacementLengths = [67.8276,67.6674,89.905,90.0772,60.367,60.2474,50.6744,50.7472,87.4533,87.42,76.2376,76.2746,77.5331,81.422,73.8853,61.3621,38.288,30.597,31.2172,39.4338,50.3752,60.5808,67.2841,68.2037,62.7788,56.1778,65.1842,97.3991,136.54,162.571,160.141,+5590 more]
  DisplacementVectors = (5621) [(67.3498,0,8.03645),(67.2407,0,7.58734),(68.4805,0,58.2523),(68.6246,0,58.3486),(15.7412,0,58.2786),(15.5134,0,58.2158),(-29.5749,0,41.1487),+5614 more]
  Eigenmode = 9
  EigenmodeFrequency = 3695.16
  MaxShear = [420.893,518.079,16.1104,18.9097,16.2449,31.8169,17.5047,12.9769,4.85593,11.0417,333.874,309.856,246.181,126.869,20.4776,40.3558,33.8414,104.338,305.915,647.698,1063.17,1617.85,2038.26,2423.22,2693.34,2127.86,889.758,1754.4,4352.62,6637.44,+5591 more]
  Mesh = -> ResultMesh
  NodeNumbers = <same value as first occurrence — deduplicated (x9 in doc)>
  NodeStrainXX = [0.0866858,0.10603,0.000356773,0.0011056,-0.00147449,-0.0013015,0.00153498,-0.000363045,-0.000704573,0.000766257,0.0662781,0.0609837,0.0526878,0.0261328,0.00107444,-0.00326225,0.00312844,-0.020315,-0.0619115,-0.1351,-0.223853,-0.33298,+5599 more]
  NodeStrainXY = [0.000126696,-0.000678998,-0.000886264,0.000558139,-0.00175602,-0.000324271,0.000435645,-0.00121141,-0.000348775,-0.000102432,-0.000586812,-0.000145766,0.000376717,0.000911084,-0.000397182,-0.000821511,-0.000920675,0.00106657,0.00132168,+5602 more]
  NodeStrainXZ = [-0.0152173,-0.0190508,-0.00214686,-0.00207128,0.000326174,-0.00454414,0.00252956,0.00149496,-1.88096e-05,0.000423376,0.0160399,0.0171919,-0.000885188,-0.00131857,-0.000457216,-0.00365906,-0.00415731,-0.00345097,-0.0117504,-0.00308834,+5601 more]
  NodeStrainYY = [2.0151e-09,3.73923e-08,0,0,-3.14722e-09,-1.73206e-10,0,0,0,0,-6.04283e-09,-1.64508e-08,-0.00010063,0.000470961,0.000526464,1.10291e-09,9.00445e-09,-0.000904226,-0.000677504,-1.30748e-09,1.84421e-08,-0.00414835,-0.000987452,-0.000491829,+5597 more]
  NodeStrainYZ = [0.000692059,-0.000944246,-0.000157512,0.00132484,0.00027872,0.000359972,0.000909905,0.000558235,0.000497862,0.00146233,0.00118608,-0.000445381,0.00013664,-0.000210902,0.00146943,0.00091765,-0.0012983,0.000532919,-0.00208442,0.00153994,+5601 more]
  NodeStrainZZ = [-0.0404344,-0.0502804,-0.00143141,-0.00223881,0.00232906,0.00246897,0.000905423,0.000768367,0.000149178,-0.0014764,-0.0322818,-0.0288954,-0.0237493,-0.0131479,-0.00441507,0.00664826,-0.00246212,0.011269,0.0299724,0.0659338,0.105542,+5600 more]
  NodeStressXX = [822.943,1001.87,-3.85375,0.632991,-4.6034,-1.69839,23.853,-0.0177662,-7.71606,0.869423,621.383,576.368,504.342,245.299,-9.18932,-1.62568,23.9593,-187.771,-585.367,-1265.86,-2118.68,-3181.56,-4087.3,-4905.52,-5336.3,-4180.51,-1310.62,+5594 more]
  NodeStressXY = [0.815842,-4.37233,-5.70701,3.59407,-11.3077,-2.08811,2.80529,-7.80072,-2.2459,-0.659602,-3.77871,-0.938646,2.42583,5.86683,-2.55761,-5.29003,-5.92859,6.86803,8.51081,-4.01137,-7.45715,20.8942,-34.6973,4.01813,-10.1726,1.55641,-1.72977,7.89,+5593 more]
  NodeStressXZ = [-97.9905,-122.676,-13.8245,-13.3378,2.10036,-29.2615,16.2888,9.62665,-0.121122,2.72629,103.287,110.705,-5.70008,-8.49077,-2.9442,-23.5621,-26.7705,-22.2221,-75.6652,-19.887,-67.4353,-371.824,-494.764,-439.351,-229.361,141.056,512.839,+5594 more]
  NodeStressYY = [264.739,319.104,-6.15115,-6.4864,4.8914,6.68249,13.9686,2.32002,-3.17903,-4.06481,194.592,183.67,164.417,80.0528,-12.7179,19.3812,3.81405,-62.7771,-191.057,-395.899,-677.204,-1064.08,-1358.93,-1618.59,-1707.49,-1298.2,-375.853,1113.46,+5593 more]
  NodeStressYZ = [4.45644,-6.08037,-1.01428,8.53118,1.79479,2.318,5.85924,3.5947,3.20593,9.4165,7.63766,-2.86799,0.879881,-1.35808,9.46225,5.90911,-8.36028,3.43167,-13.4224,9.91631,-24.9953,30.7532,-2.29577,-12.8053,1.13986,-1.74494,4.95677,16.56,4.95791,+5592 more]
  NodeStressZZ = [4.36607,-4.67151,-15.3686,-20.903,19.8891,22.5812,19.799,7.26784,-2.21842,-13.5719,-13.2835,-2.399,12.1337,-7.64426,-44.5384,62.192,-12.0406,15.6108,6.30908,28.6743,2.4223,-33.508,-133.144,-139.52,30.78,65.8455,143.526,176.486,97.4017,+5592 more]
  PrincipalMax = [834.51,1016.62,6.77552,7.02418,20.1366,42.3882,39.6441,14.1766,0.839983,2.3705,637.784,596.826,504.425,245.794,-6.30783,70.9746,38.2702,18.0993,16.8272,29.2139,5.46114,10.5493,-72.1737,-99.2439,40.5653,70.5281,306.22,3515.42,8738.79,13254,+5591 more]
  PrincipalMed = [264.814,319.212,-6.70366,-2.98532,12.3937,6.42279,13.3416,7.17068,-5.08161,0.575184,194.872,183.699,164.405,79.8575,-12.8747,18.7099,6.87513,-62.4604,-191.939,-396.116,-678.054,-1064.54,-1358.5,-1618.7,-1707.46,-1298.2,-375.87,1113.59,+5593 more]
  PrincipalMin = [-7.27592,-19.5344,-25.4454,-30.7953,-12.3532,-21.2457,4.63483,-11.7772,-8.87188,-19.713,-29.9643,-22.8856,12.0623,-7.94429,-47.2631,-9.73699,-29.4126,-190.576,-595.004,-1266.18,-2120.87,-3225.15,-4148.7,-4945.69,-5346.11,-4185.19,-1473.3,+5594 more]
  ResultType = Fem::ResultMechanical
  Stats = [-77.2026,68.6246,-0.486995,0.733141,-144.805,164.003,7.89607,166.963,8.47797,14165.5,-1929.91,15985.5,-4151.31,5108.5,-13789,3607.92,4.85593,8008.62,0,0,0,0,0,0,0,0]
  Time = 0
  vonMises = [744.04,915.084,28.0279,33.9403,29.3934,55.2645,31.5696,23.2562,8.47797,21.2428,588.477,546.531,436.602,223.19,38.0987,70.9056,58.666,182.276,538.693,1143.67,1880.18,2854.28,3609.56,4293.34,4759.81,3762.93,1555.04,3106.91,7704.53,11741,+5591 more]
FEATURE [Fem::FemResultObjectPython] CCX_EigenMode_10_Results  # FEM object (typed FeaturePython)
  DisplacementLengths = [31.06,30.9489,80.6691,80.7626,83.4215,83.4972,74.3624,74.3678,78.9128,78.9652,40.4638,40.5333,45.6343,60.1584,68.9094,67.1517,52.0155,34.7971,31.8468,43.6598,57.9072,67.0669,66.37,51.9158,27.5866,46.2492,101.577,152.146,172.79,144.534,+5591 more]
  DisplacementVectors = (5621) [(30.6768,0,4.86369),(30.6002,0,4.63249),(32.6931,0,73.7473),(32.7533,0,73.8229),(-38.9287,0,73.7814),(-39.0898,0,73.7819),(-32.6204,0,-66.8257),+5614 more]
  Eigenmode = 10
  EigenmodeFrequency = 5074.03
  MaxShear = [842.297,908.55,33.5477,34.2234,51.3125,65.0759,29.7211,25.0414,29.7008,24.6184,634.818,616.144,471.484,147.116,68.592,73.0101,170.196,639.552,1295.29,2263.95,3327.97,4541.49,5320.24,5616.13,4946.41,2870.05,1868.44,5557.96,8449.79,8248.96,+5591 more]
  Mesh = -> ResultMesh
  NodeNumbers = <same value as first occurrence — deduplicated (x9 in doc)>
  NodeStrainXX = [0.173503,0.186645,-0.000307582,6.63269e-05,-0.00192595,-0.00146116,0.000626046,-0.000719606,-0.000170609,0.000438926,-0.124355,-0.121624,-0.100292,-0.0307326,-0.00301359,0.00497454,0.0351326,0.13322,0.27312,0.474886,0.703165,0.952421,+5599 more]
  NodeStrainXY = [-2.70049e-05,-0.00134329,0.000242879,-0.000336003,-0.00102826,-0.000154928,-0.00141878,0.000287013,0.000653792,-0.000978014,0.000238447,-0.000891977,0.000172408,0.000534327,-0.000709938,0.00171529,-0.000743409,-0.000541512,-0.00401087,+5602 more]
  NodeStrainXZ = [-0.0284113,-0.0292624,-0.00503803,-0.00494842,-0.00690635,-0.00949148,-0.00401717,-0.00382177,-0.00426847,-0.0036539,-0.0335834,-0.0303918,0.00255589,0.00539168,0.00875708,0.00686992,0.00733225,0.0111609,0.0189855,0.0123667,0.0221473,+5600 more]
  NodeStrainYY = [-5.09416e-10,2.14186e-08,0,0,-3.49637e-09,-1.47312e-10,0,0,0,0,-2.5085e-10,-5.74916e-09,-0.00026968,0.000770879,0.000436969,2.83037e-10,8.99567e-10,-0.000315503,-0.000501405,1.25141e-08,-1.14668e-09,0.00493699,0.00124561,0.000183176,+5597 more]
  NodeStrainYZ = [0.000423122,-0.00115412,-0.000415345,0.000944901,0.000203324,0.000233641,0.000544172,-0.000209796,0.000781335,0.000199777,-0.000690025,0.00071195,0.000604017,0.000599142,-0.000319018,-0.00085749,0.00116574,-0.000573576,0.00124572,+5602 more]
  NodeStrainZZ = [-0.0818572,-0.0893786,-0.0027205,-0.00313629,0.00571754,0.00545998,-0.00256831,-0.00186877,0.0024853,0.00147541,0.0610112,0.0598168,0.046048,0.0136296,0.00901491,-0.0126035,-0.0155453,-0.0641527,-0.127313,-0.227802,-0.329423,-0.444979,+5599 more]
  NodeStressXX = [1641.82,1758.62,-19.3131,-17.145,9.30074,13.4799,-7.086,-19.4495,12.1505,13.7839,-1163.34,-1136.96,-957.849,-291.383,17.4465,-11.6347,338.348,1251.38,2590.44,4472.26,6667.22,9065.82,10702.4,11256,9711.19,5050.17,-2466.57,-10923.1,-16779.8,+5592 more]
  NodeStressXY = [-0.173895,-8.64998,1.56399,-2.16365,-6.62139,-0.99764,-9.13605,1.84819,4.21003,-6.29781,1.53545,-5.74379,1.1102,3.44075,-4.57157,11.0454,-4.7871,-3.48701,-25.8276,18.9054,15.7828,-30.9873,52.4887,18.5925,7.87949,-1.54022,-15.8181,-18.0202,+5593 more]
  NodeStressXZ = [-182.952,-188.432,-32.4418,-31.8648,-44.4727,-61.1194,-25.8681,-24.6099,-27.4864,-23.5289,-216.257,-195.704,16.4584,34.7192,56.3903,44.2381,47.2153,71.8693,122.255,79.6343,142.615,615.22,650.462,282.405,-379.073,-1081.15,-1519.52,-1380.92,+5593 more]
  NodeStressYY = [524.57,556.742,-17.3325,-17.5722,21.7027,22.8889,-11.1174,-14.8156,13.2491,10.9575,-362.573,-353.776,-313.767,-88.5196,39.666,-43.6677,112.116,391.496,828.486,1414.29,2139.26,2964.6,3480.85,3615.64,3060.52,1527.39,-891.507,-3551.2,-5339.11,+5592 more]
  NodeStressYZ = [2.72465,-7.43182,-2.67457,6.08459,1.30928,1.5045,3.50414,-1.35096,5.03132,1.28645,-4.44334,4.58453,3.88951,3.85811,-2.05429,-5.52172,7.50667,-3.69348,8.02167,-12.2461,33.9126,-45.8294,10.8166,9.99323,5.6576,9.69409,1.79479,-15.4655,+5593 more]
  NodeStressZZ = [-2.54128,-18.8015,-34.8508,-37.7679,58.5202,58.0478,-27.6557,-26.8494,29.2529,20.4582,30.3019,31.4076,-15.5093,-5.71734,94.9028,-124.827,12.0131,-19.5772,11.897,-52.6206,17.9762,67.415,142.162,38.0254,-152.514,-267.033,-292.297,-155.859,+5593 more]
  PrincipalMax = [1661.93,1778.43,6.62463,7.19113,85.0578,100.861,14.0812,2.0459,49.5555,41.7392,68.3241,63.3881,-15.1708,-1.35189,124.766,5.15107,345.1,1255.45,2596.59,4473.78,6670.34,9107.88,10742.7,11263.2,9725.75,5261.6,488.993,18.4736,98.9358,300.01,+5591 more]
  PrincipalMed = [524.583,556.807,-17.6503,-18.4206,22.033,22.8472,-14.5792,-15.1235,14.9429,10.9579,-362.622,-353.817,-313.816,-88.6837,39.6663,-44.4113,112.669,391.51,828.224,1414.28,2139.73,2965.06,3480.48,3615.62,3060.52,1527.43,-891.489,-3551.2,+5593 more]
  PrincipalMin = [-22.6639,-38.6739,-60.4707,-61.2557,-17.5671,-29.2912,-45.361,-48.0369,-9.84598,-7.49757,-1201.31,-1168.9,-958.138,-295.584,-12.4175,-140.869,4.70741,-23.6577,6.00988,-54.1294,14.3885,24.9,102.23,30.8952,-167.072,-478.5,-3247.88,-11097.4,+5593 more]
  ResultType = Fem::ResultMechanical
  Stats = [-39.1238,42.0597,-3.81899,2.43156,-174.104,180.256,0.964755,180.39,40.0409,40916.8,-5879.88,73652.9,-9099.72,32963.4,-29207.7,32512.5,22.9362,20570.2,0,0,0,0,0,0,0,0]
  Time = 0
  vonMises = [1488.44,1604.49,58.8415,59.8989,89.6442,113.455,51.4894,44.0816,51.6772,43.0834,1118.28,1085.58,834.724,261.732,119.946,128.613,301.287,1130.23,2292.84,4001.17,5888.34,8027.43,9417.33,9937.27,8738.15,5045.62,3272.81,9829.85,14942.1,14574.7,+5591 more]
FEATURE [Fem::FemResultObjectPython] CCX_EigenMode_11_Results  # FEM object (typed FeaturePython)
  DisplacementLengths = [36.8558,36.5039,83.1637,83.9419,82.18,82.4978,78.2227,77.2495,79.8644,79.4264,40.8423,40.7211,43.9686,59.3363,69.0369,68.4028,54.7833,38.9899,38.8774,50.6467,61.3163,63.0767,51.4582,28.842,44.1551,96.8097,141.869,151.767,106.666,29.4824,+5591 more]
  DisplacementVectors = (5621) [(36.8004,0,-2.0197),(36.2895,0,-3.9501),(40.1269,0,72.8425),(40.7478,0,73.3884),(-37.8343,0,72.9528),(-38.881,0,72.7609),(39.3994,0,67.5757),+5614 more]
  Eigenmode = 11
  EigenmodeFrequency = 6722.28
  MaxShear = [1266.03,1675.66,69.2448,82.7828,76.313,132.4,86.4107,65.1023,23.1065,55.7118,1196.22,1113.61,800.499,374.676,108.999,204.622,294.421,1167.3,2313.17,3853.17,5291.21,6380.27,6498.2,5711.15,3679.45,2686.56,7081.93,10300.7,8860.33,3227.85,+5591 more]
  Mesh = -> ResultMesh
  NodeNumbers = <same value as first occurrence — deduplicated (x9 in doc)>
  NodeStrainXX = [0.261502,0.343688,0.00212113,0.00555876,-0.00707378,-0.00633112,0.00704879,-0.00172493,-0.00326528,0.00358994,0.238388,0.219119,0.171495,0.0757097,0.00600116,-0.0161703,-0.0570114,-0.240516,-0.48186,-0.80938,-1.11658,-1.3426,-1.38236,+5598 more]
  NodeStrainXY = [0.00100089,-0.00169314,-0.00422681,0.0026964,-0.00806229,-0.00157054,0.00228999,-0.00576475,-0.00184621,-0.000268045,-0.00198018,-0.00133123,0.00188931,0.00413272,-0.0017107,-0.00415767,-0.00417796,0.00495749,0.00501585,-0.00210696,+5601 more]
  NodeStrainXZ = [-0.0447693,-0.0622161,-0.00884498,-0.00847571,0.00376845,-0.0186324,0.0126413,0.00766225,0.000985773,0.00289969,0.0540363,0.0603513,-0.00891336,-0.00727183,-0.00405552,-0.0187912,-0.0216185,-0.0170882,-0.0490678,-0.0100167,-0.0279422,+5600 more]
  NodeStrainYY = [1.11845e-08,1.7041e-07,0,0,-1.42503e-08,-7.23193e-10,0,0,0,0,-2.29451e-08,-6.75085e-08,-0.000441861,0.00207656,0.0024259,4.08173e-09,4.02193e-08,-0.00423252,-0.00299811,-5.3282e-09,6.67728e-08,-0.00947464,0.000305052,0.0029833,-0.000745335,+5596 more]
  NodeStrainYZ = [0.00365574,-0.00317168,-0.000589315,0.0060195,0.00125652,0.0017134,0.0042509,0.00267299,0.00224189,0.00687906,0.00536926,-0.00307374,0.000898025,-0.00120767,0.00710283,0.00454226,-0.00618774,0.00242595,-0.00867844,0.00520751,-0.0119982,+5600 more]
  NodeStrainZZ = [-0.121268,-0.161586,-0.00639939,-0.0100821,0.00988689,0.0104834,0.0048328,0.00404492,9.99807e-06,-0.00746142,-0.11681,-0.104921,-0.0764588,-0.0394872,-0.0234683,0.0337602,0.0220036,0.12027,0.229462,0.387126,0.525584,0.628379,0.633464,+5598 more]
  NodeStressXX = [2486.59,3255.48,-10.8295,9.90362,-29.4489,-17.0012,113.399,2.1719,-39.6593,0.957026,2230.98,2064.65,1645.77,706.745,-47.4506,-3.44424,-567.5,-2261.29,-4564.76,-7628.85,-10572.9,-12788,-13186.5,-11372.4,-6204.19,3440.41,13900.9,20532.2,+5593 more]
  NodeStressXY = [6.44512,-10.9028,-27.2181,17.3632,-51.9163,-10.1134,14.7461,-37.1215,-11.8885,-1.72605,-12.7511,-8.57232,12.166,26.6122,-11.0159,-26.7729,-26.9035,31.9232,32.299,-13.5675,-9.98709,24.892,-107.833,24.1279,10.6185,73.8571,45.6133,73.7887,+5593 more]
  NodeStressXZ = [-288.287,-400.634,-56.9563,-54.5784,24.2665,-119.982,81.4024,49.3402,6.34778,18.6723,347.961,388.626,-57.3967,-46.8261,-26.1151,-121.004,-139.21,-110.038,-315.967,-64.5015,-179.931,-655.356,-305.394,585.858,1531.57,2225.65,1952.77,659.438,+5593 more]
  NodeStressYY = [802.682,1042.34,-24.4883,-25.8914,16.1018,23.7673,68.0091,13.2794,-18.6329,-22.16,695.905,653.656,538.604,232.592,-70.4731,100.683,-200.381,-739.762,-1481.17,-2416.94,-3382.81,-4203.4,-4282.92,-3617.25,-1835.9,1293.32,4497.44,6471.9,5267.4,+5592 more]
  NodeStressYZ = [23.5407,-20.4237,-3.79483,38.762,8.0912,11.0332,27.3732,17.2125,14.4364,44.297,34.5748,-19.793,5.78274,-7.77667,45.7379,29.2494,-39.8453,15.6217,-55.8839,33.5332,-77.2614,64.5635,-2.84092,-33.541,10.901,40.6973,81.8343,124.887,33.7553,+5592 more]
  NodeStressZZ = [21.7865,1.81971,-65.6965,-90.8142,79.7675,91.2741,99.1294,39.3263,-18.5685,-70.207,-56.2781,-21.9738,49.1007,-35.0533,-237.216,318.078,-58.6912,61.9578,15.7265,75.9162,1.62744,-96.0133,-205.759,-10.7352,486.802,434.861,287.774,-24.1479,+5593 more]
  PrincipalMax = [2519.87,3304.12,32.9755,33.8092,85.0944,170.253,194.812,74.5272,-3.66193,11.9762,2282.78,2134.78,1647.96,711.218,-33.455,363.534,-17.4497,67.4043,39.6291,76.9101,6.44119,-61.2992,-198.578,19.6805,820.778,4625.26,14175.8,20553.8,17225.3,+5592 more]
  PrincipalMed = [803.388,1042.74,-28.4757,-8.85479,48.8575,22.3344,63.7354,35.9277,-23.3239,-3.93877,697.485,653.992,538.554,231.201,-70.2325,97.4924,-202.83,-739.311,-1483.12,-2417.36,-3384.55,-4204.27,-4281.61,-3617.45,-1835.95,1291.19,4498.35,6473.77,+5593 more]
  PrincipalMin = [-12.1971,-47.2133,-105.514,-131.756,-67.5315,-94.5476,21.9904,-55.6774,-49.8748,-99.4474,-109.658,-92.436,46.9615,-38.1351,-251.452,-45.7097,-606.293,-2267.19,-4586.71,-7629.42,-10576,-12821.8,-13195,-11402.6,-6538.12,-747.854,11.9487,+5594 more]
  ResultType = Fem::ResultMechanical
  Stats = [-44.6905,40.7478,-2.59222,1.59192,-181.256,172.356,0.843276,181.352,40.1695,25040.8,-3781.88,50358.1,-7931.16,26920.1,-24795.3,23975,23.1065,13721.6,0,0,0,0,0,0,0,0]
  Time = 0
  vonMises = [2238.62,2960.85,120.188,148.891,138.12,229.849,156.19,115.833,40.1695,104.38,2108.13,1963.46,1420.5,657.453,202.134,359.698,521.481,2053.72,4083.75,6810.82,9359.57,11275.2,11511.4,10107.1,6454.53,4698.09,12537.9,18237.2,15656,5638.63,11840,+5590 more]
FEATURE [Fem::FemResultObjectPython] CCX_EigenMode_12_Results  # FEM object (typed FeaturePython)
  DisplacementLengths = [36.1241,36.1021,83.9817,83.9101,87.103,87.1356,78.9867,79.0607,78.8839,78.9317,41.2603,41.207,42.2981,57.4864,67.4782,67.4312,55.4837,40.5489,42.2294,53.1245,59.5577,53.8725,35.2671,37.733,82.7726,125.639,133.972,87.0913,37.8642,131.093,+5591 more]
  DisplacementVectors = (5621) [(-34.5822,0,10.4415),(-34.436,0,10.8409),(-40.4102,0,-73.6202),(-40.4233,0,-73.5314),(46.4293,0,-73.697),(46.6837,0,-73.5747),(43.0407,0,66.2299),+5614 more]
  Eigenmode = 12
  EigenmodeFrequency = 8545.34
  MaxShear = [2349.54,2434.97,89.5424,90.2776,159.67,168.999,84.6986,70.7798,71.9254,64.5525,1729.57,1696.8,1303.78,439.875,184.883,212.126,540.32,1853.79,3470.75,5522.83,7199.53,7986.29,7212.08,4785.5,3059.38,7970.91,11890.6,10438,3567.51,9912.65,+5591 more]
  Mesh = -> ResultMesh
  NodeNumbers = <same value as first occurrence — deduplicated (x9 in doc)>
  NodeStrainXX = [-0.484578,-0.501935,0.000923271,0.000733381,0.00518761,0.00396897,-0.000581988,0.000846334,0.000174962,6.18878e-05,0.340678,0.33542,0.277639,0.0915537,0.00826246,-0.0140313,-0.111838,-0.387063,-0.732948,-1.16206,-1.52297,-1.69131,-1.51738,+5598 more]
  NodeStrainXY = [8.44733e-05,0.00298226,-0.00214553,0.00200302,0.000894087,0.000133724,0.00381668,-0.00187384,-0.002043,0.0023326,-0.000807719,0.00133653,-0.000442312,-0.000558341,0.0014404,-0.00510739,0.00103096,0.00216868,0.00853885,-0.00680816,+5601 more]
  NodeStrainXZ = [0.0758768,0.0725577,0.0132513,0.0133009,0.0224048,0.0244411,0.0118286,0.010448,0.0103211,0.00924654,0.0888727,0.0840435,-0.00909597,-0.0150347,-0.0227883,-0.0206001,-0.023072,-0.0297873,-0.0473323,-0.0266187,-0.0327516,-0.0578662,0.0821836,+5598 more]
  NodeStrainYY = [4.33054e-09,-1.44723e-08,0,0,6.60558e-09,6.09732e-10,0,0,0,0,-5.5488e-09,3.33847e-09,0.000585014,-0.00134316,-0.000618149,-8.73406e-10,4.02938e-09,-0.000222597,0.000578437,-2.63611e-08,-3.39018e-09,-0.00252017,0.00177439,0.00443591,+5597 more]
  NodeStrainYZ = [-0.000723339,0.00194481,0.00101621,-0.00119173,-0.000299254,-0.000332952,-0.000298157,0.000924846,-0.00133873,0.0008251,0.00264512,-0.0028536,-0.00101684,-0.00170735,0.0024377,0.00286892,-0.00378246,0.00175411,-0.00298985,0.00350258,+5601 more]
  NodeStrainZZ = [0.229208,0.240249,0.00730981,0.00771389,-0.0159749,-0.0151415,0.00744607,0.00567334,-0.00630165,-0.00538167,-0.166204,-0.164005,-0.126881,-0.0416391,-0.0263105,0.0359311,0.0492097,0.185583,0.340731,0.552373,0.712067,0.786408,0.716504,+5598 more]
  NodeStressXX = [-4582.1,-4730.02,53.0707,53.0739,-28.3401,-38.3929,35.5417,42.7679,-33.9419,-30.0514,3192.43,3141.06,2654.1,867.569,-53.6385,34.9998,-1078.65,-3646.98,-6961.45,-10972.8,-14448.6,-16085,-14344.9,-8330.37,2701.49,15434.9,23612.5,20105.8,+5593 more]
  NodeStressXY = [0.543957,19.204,-13.8159,12.8982,5.75738,0.861101,24.5771,-12.0664,-13.1557,15.0206,-5.20122,8.60646,-2.84822,-3.59538,9.2753,-32.8885,6.63877,13.965,54.985,-43.8404,-7.66705,7.3016,-62.5171,-1.43906,48.1458,71.3359,66.8264,40.5578,-2.823,+5592 more]
  NodeStressXZ = [488.6,467.228,85.3305,85.6497,144.274,157.386,76.1689,67.279,66.4618,59.5421,572.286,541.189,-58.5725,-96.8144,-146.743,-132.652,-148.569,-191.812,-304.791,-171.409,-210.9,-372.623,529.212,1898.05,2868.39,2674.86,1040.98,-1386.05,-3069.78,+5592 more]
  NodeStressYY = [-1461.71,-1497.87,47.1254,48.3514,-61.7452,-63.9507,39.2894,37.318,-35.0686,-30.4499,998.67,981.162,870.04,269.369,-110.824,125.353,-358.481,-1155.96,-2237.98,-3489.82,-4641.54,-5210.22,-4562.53,-2482.21,1058.03,5048.81,7502.87,6214.84,+5593 more]
  NodeStressYZ = [-4.65787,12.5234,6.54378,-7.67402,-1.92702,-2.14401,-1.91995,5.95545,-8.6206,5.31315,17.033,-18.3755,-6.5478,-10.9943,15.6973,18.4741,-24.3568,11.2954,-19.2528,22.5545,-49.2255,30.6318,-16.9093,-0.829888,8.85539,37.7073,58.5715,59.4535,+5593 more]
  NodeStressZZ = [14.2443,49.1912,94.1961,98.0242,-164.614,-161.453,87.2375,73.8509,-75.6474,-65.1046,-71.5858,-74.9325,49.2352,9.88781,-276.268,356.728,-41.6001,40.5144,-47.6057,67.1273,-56.2578,-129.998,39.897,455.631,575.463,418.216,-76.7006,-584.618,+5593 more]
  PrincipalMax = [65.6231,94.5689,161.509,164.127,63.195,69.065,143.429,127.451,19.3917,19.1691,3289.86,3229.7,2655.42,878.371,19.2464,407.264,-18.8888,50.5574,-33.9825,69.9396,-52.6425,-121.118,59.42,848.135,4698.05,15897.7,23658.5,20198.3,4769.97,244.049,+5591 more]
  PrincipalMed = [-1461.72,-1497.9,50.4587,51.7511,-61.7487,-63.9277,44.6069,40.5933,-39.5906,-34.8391,998.935,981.481,870.089,269.834,-109.458,126.804,-360.314,-1155.97,-2237.58,-3489.72,-4642.06,-5210.4,-4562.22,-2482.21,1057.65,5048.39,7502.98,6215.3,+5593 more]
  PrincipalMin = [-4633.47,-4775.37,-17.5756,-16.4284,-256.146,-268.934,-25.9677,-14.108,-124.459,-109.936,-169.285,-163.894,47.8657,-1.37844,-350.519,-16.9879,-1099.53,-3657.02,-6975.48,-10975.7,-14451.7,-16093.7,-14364.7,-8722.87,-1420.72,-44.1404,+5595 more]
  ResultType = Fem::ResultMechanical
  Stats = [-47.1705,46.7177,-1.66673,2.61281,-178.251,174.674,0.886346,178.298,112.304,28505.2,-24661.9,31972.1,-28434.9,10291.6,-51104.8,3534.53,64.5525,16125.7,0,0,0,0,0,0,0,0]
  Time = 0
  vonMises = [4151.76,4300.81,156.576,157.919,278.729,294.922,147.381,123.644,125.249,112.304,3047.85,2990.22,2308.98,780.331,325.116,373.714,956.763,3275.44,6143.61,9765.19,12740.2,14132.8,12757.4,8415.5,5330.77,14102.9,21032.1,18423.4,6197.27,17514.4,+5591 more]
FEATURE [App::TextDocument] ccx_dat_file
  Text = <blob: 5813 chars omitted>
FEATURE [Fem::FemPostWarpVectorFilter] WarpVector
  Factor = 0
  Vector = 0
FEATURE [Fem::FemPostDataAtPointFilter] DataAtPoint
  Center = (365.83,-30,18.75)
  FieldName = Displacement Magnitude
  Input = -> WarpVector
  PointData = [0.00831516,0.00831516,0.00831516,0.00831516,0.00831516,0.00831516,0.00831516,0.00831516,0.00831516,0.00831516]
  Radius = 0
  Unit = m
FEATURE [Fem::FemPostPipeline] ResultPipeline
  Filter = -> [WarpVector,DataAtPoint]
  Mode = 2
FEATURE [Fem::FemPostDataAtPointFilter] DataAtPoint001
  Center = (209.545,-35.2534,22.2834)
  PointData = [0]
  Radius = 0
FEATURE [Fem::FemPostWarpVectorFilter] WarpVector001
  Factor = 0
  Vector = 0
FEATURE [Fem::FemPostPipeline] ResultPipeline001
  Filter = -> [DataAtPoint001,WarpVector001]
  Mode = 2
FEATURE [Fem::FemPostWarpVectorFilter] WarpVector002
  Factor = 0
  Vector = 0
FEATURE [Fem::FemPostDataAtPointFilter] DataAtPoint002
  Center = (395.15,-30,18.29)
  FieldName = Displacement
  PointData = [0.00105714,0.00105714,0.00105714,0.00105714,0.00105714,0.00105714,0.00105714,0.00105714,0.00105714,0.00105714]
  Radius = 0
  Unit = m
FEATURE [Fem::FemPostPipeline] ResultPipeline002
  Filter = -> [WarpVector002,DataAtPoint002]
  Mode = 2
FEATURE [Fem::FemAnalysis] Analysis
  Group = -> [SolverCcxTools,MaterialSolid,FemConstraintDisplacement,FEMMeshNetgen,CCX_EigenMode_4_Results,CCX_EigenMode_5_Results,CCX_EigenMode_6_Results,CCX_EigenMode_7_Results,CCX_EigenMode_8_Results,CCX_EigenMode_9_Results,CCX_EigenMode_10_Results,CCX_EigenMode_11_Results,CCX_EigenMode_12_Results,ccx_dat_file,ResultPipeline,ResultPipeline001,ResultPipeline002]
